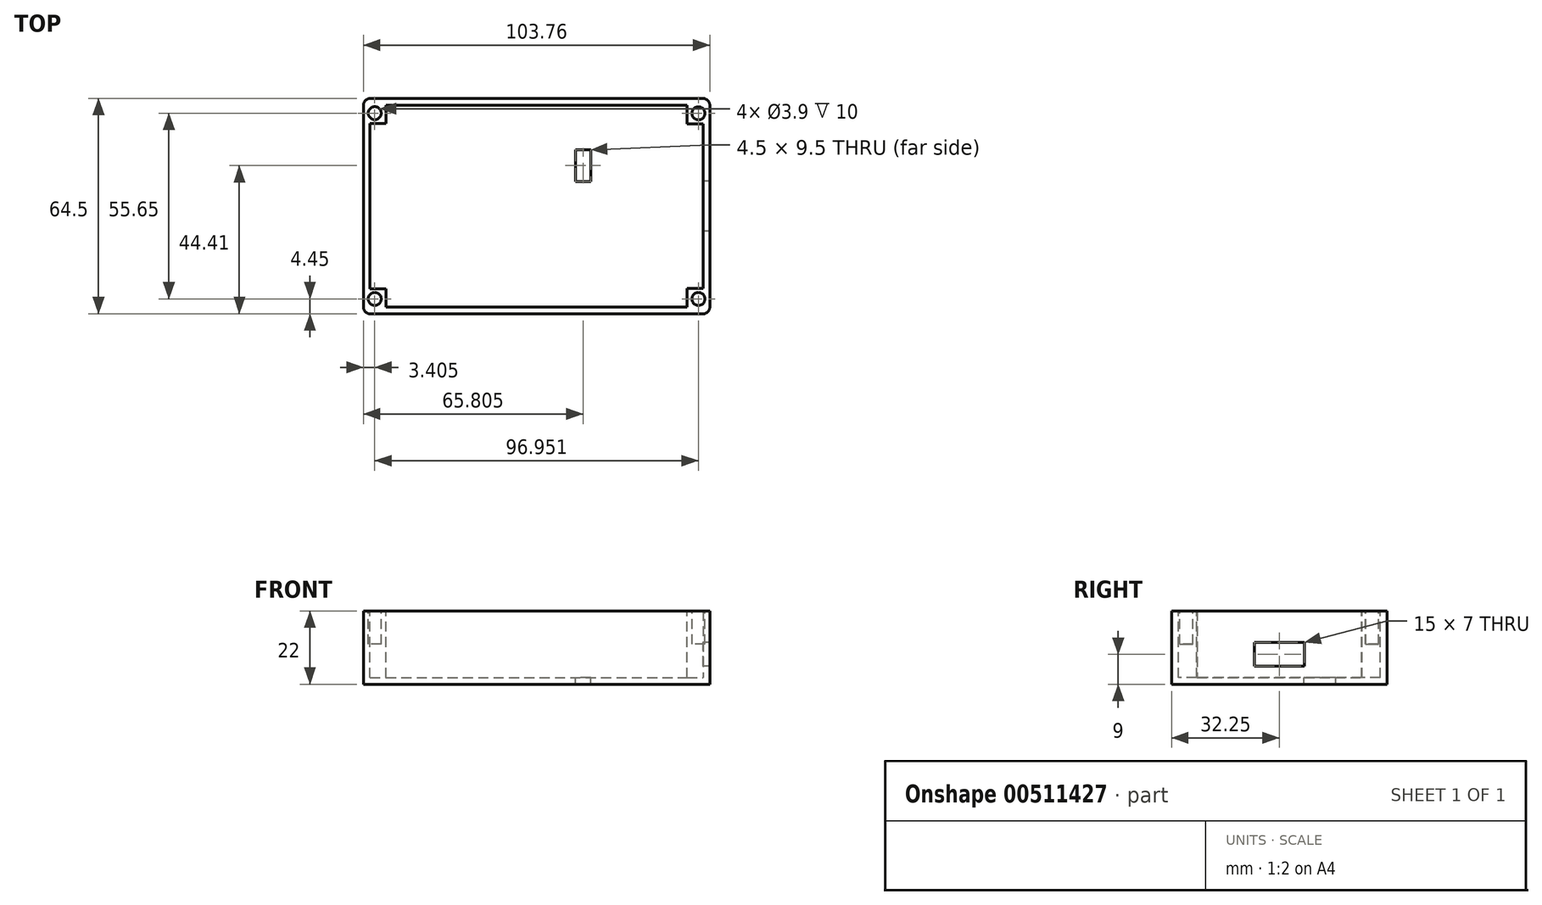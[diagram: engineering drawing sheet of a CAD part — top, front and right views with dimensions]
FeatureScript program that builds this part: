
annotation { "Feature Type Name" : "Feature", "Feature Type Description" : "" }
export const myFeature = defineFeature(function(context is Context, id is Id, definition is map)
    precondition{}
    {
        {
            var Q0;
            Q0=qCreatedBy(makeId("Top.planeOp"),FACE);
            var sketch = newSketch(context, id + "F0", { "sketchPlane" : qUnion([Q0])});
            skLineSegment(sketch, "E0.bottom", {"start": v(-51.88, 32.25) * mm, "end": v(51.88, 32.25) * mm});
            skLineSegment(sketch, "E0.top", {"start": v(-51.88, -32.25) * mm, "end": v(51.88, -32.25) * mm});
            skLineSegment(sketch, "E0.left", {"start": v(-51.88, 32.25) * mm, "end": v(-51.88, -32.25) * mm});
            skLineSegment(sketch, "E0.right", {"start": v(51.88, 32.25) * mm, "end": v(51.88, -32.25) * mm});
            skPoint(sketch, "E0.middle", {"position": v(0, 0) * mm});
            skPoint(sketch, "E1", {"position": v(-51.88, 0) * mm});
            skSolve(sketch);
        }
        {
            var Q0;
            Q0=makeQuery(id+"F0.imprint","IMPRINT",FACE,{"disambiguationData":[TD([[makeQuery(id+"F0.imprint","IMPRINT",EDGE,{"derivedFrom":sQuery(id+"F0.wireOp",EDGE,"E0.bottom")}),-1.0]])]});
            extrude(context, id + "F1", {"entities" : qUnion([Q0]), "depth" : 22 * mm});
        }
        {
            var Q0;
            Q0=makeQuery(id+"F1.opExtrude","CAP_FACE",FACE,{"disambiguationData":[OSD([sQuery(id+"F0.wireOp",EDGE,"E0.bottom"),sQuery(id+"F0.wireOp",EDGE,"E0.top"),sQuery(id+"F0.wireOp",EDGE,"E0.left"),sQuery(id+"F0.wireOp",EDGE,"E0.right")])],"isStart":false});
            shell(context, id + "F2", {"entities" : qUnion([Q0]), "thickness" : 2 * mm});
        }
        {
            var Q0;
            Q0=qCreatedBy(makeId("Right.planeOp"),FACE);
            var sketch = newSketch(context, id + "F3", { "sketchPlane" : qUnion([Q0])});
            skLineSegment(sketch, "E2.bottom", {"start": v(7.5, 12.5) * mm, "end": v(-7.5, 12.5) * mm});
            skLineSegment(sketch, "E2.top", {"start": v(7.5, 5.5) * mm, "end": v(-7.5, 5.5) * mm});
            skLineSegment(sketch, "E2.left", {"start": v(7.5, 12.5) * mm, "end": v(7.5, 5.5) * mm});
            skLineSegment(sketch, "E2.right", {"start": v(-7.5, 12.5) * mm, "end": v(-7.5, 5.5) * mm});
            skPoint(sketch, "E3", {"position": v(7.5, 9) * mm});
            skPoint(sketch, "E4", {"position": v(0, 5.5) * mm});
            skSolve(sketch);
        }
        {
            var Q0;
            Q0=qSketchRegion(id+"F3",true);
            extrude(context, id + "F4", {"entities" : qUnion([Q0]), "operationType" : NewBodyOperationType.REMOVE, "depth" : 381 * mm});
        }
        {
            var Q0;
            Q0=makeQuery(id+"F1.opExtrude","SWEPT_EDGE",EDGE,{"disambiguationData":[OSD([sQuery(id+"F0.wireOp",EDGE,"E0.bottom"),sQuery(id+"F0.wireOp",EDGE,"E0.left")])]});
            var Q1;
            Q1=makeQuery(id+"F1.opExtrude","SWEPT_EDGE",EDGE,{"disambiguationData":[OSD([sQuery(id+"F0.wireOp",EDGE,"E0.top"),sQuery(id+"F0.wireOp",EDGE,"E0.left")])]});
            var Q2;
            Q2=makeQuery(id+"F1.opExtrude","SWEPT_EDGE",EDGE,{"disambiguationData":[OSD([sQuery(id+"F0.wireOp",EDGE,"E0.top"),sQuery(id+"F0.wireOp",EDGE,"E0.right")])]});
            var Q3;
            Q3=makeQuery(id+"F1.opExtrude","SWEPT_EDGE",EDGE,{"disambiguationData":[OSD([sQuery(id+"F0.wireOp",EDGE,"E0.bottom"),sQuery(id+"F0.wireOp",EDGE,"E0.right")])]});
            fillet(context, id + "F5", {"entities" : qUnion([Q0, Q1, Q2, Q3]), "radius" : 2 * mm, "tangentPropagation" : true, "allowEdgeOverflow" : false});
        }
        {
            var Q0;
            Q0=qCreatedBy(makeId("Top.planeOp"),FACE);
            var sketch = newSketch(context, id + "F6", { "sketchPlane" : qUnion([Q0])});
            skPoint(sketch, "E5", {"position": v(-49.87, 0) * mm});
            skLineSegment(sketch, "E6.bottom", {"start": v(16.18, 16.9) * mm, "end": v(11.68, 16.9) * mm});
            skLineSegment(sketch, "E6.top", {"start": v(16.18, 7.4) * mm, "end": v(11.68, 7.4) * mm});
            skLineSegment(sketch, "E6.left", {"start": v(16.18, 16.9) * mm, "end": v(16.18, 7.4) * mm});
            skLineSegment(sketch, "E6.right", {"start": v(11.68, 16.9) * mm, "end": v(11.68, 7.4) * mm});
            skLineSegment(sketch, "E7", {"start": v(11.68, 16.9) * mm, "end": v(-49.87, 16.9) * mm});
            skSolve(sketch);
        }
        {
            var Q0;
            Q0=qSketchRegion(id+"F6",true);
            extrude(context, id + "F7", {"entities" : qUnion([Q0]), "operationType" : NewBodyOperationType.REMOVE, "endBound" : BoundingType.SYMMETRIC, "oppositeDirection" : true, "depth" : 25.4 * mm});
        }
        {
            var Q0;
            Q0=makeQuery(id+"F1.opExtrude","CAP_FACE",FACE,{"disambiguationData":[OSD([sQuery(id+"F0.wireOp",EDGE,"E0.bottom"),sQuery(id+"F0.wireOp",EDGE,"E0.top"),sQuery(id+"F0.wireOp",EDGE,"E0.left"),sQuery(id+"F0.wireOp",EDGE,"E0.right")])],"isStart":false});
            var sketch = newSketch(context, id + "F8", { "sketchPlane" : qUnion([Q0])});
            skLineSegment(sketch, "E8.bottom", {"start": v(-49.88, 30.25) * mm, "end": v(-45.08, 30.25) * mm});
            skLineSegment(sketch, "E8.top", {"start": v(-49.88, 24.75) * mm, "end": v(-45.08, 24.75) * mm});
            skLineSegment(sketch, "E8.left", {"start": v(-49.88, 30.25) * mm, "end": v(-49.88, 24.75) * mm});
            skLineSegment(sketch, "E8.right", {"start": v(-45.08, 30.25) * mm, "end": v(-45.08, 24.75) * mm});
            skLineSegment(sketch, "E9.bottom", {"start": v(45.08, 30.25) * mm, "end": v(49.88, 30.25) * mm});
            skLineSegment(sketch, "E9.top", {"start": v(45.08, 24.65) * mm, "end": v(49.88, 24.65) * mm});
            skLineSegment(sketch, "E9.left", {"start": v(45.08, 30.25) * mm, "end": v(45.08, 24.65) * mm});
            skLineSegment(sketch, "E9.right", {"start": v(49.88, 30.25) * mm, "end": v(49.88, 24.65) * mm});
            skLineSegment(sketch, "E10.bottom", {"start": v(-49.88, -24.75) * mm, "end": v(-45.08, -24.75) * mm});
            skLineSegment(sketch, "E10.top", {"start": v(-49.88, -30.25) * mm, "end": v(-45.08, -30.25) * mm});
            skLineSegment(sketch, "E10.left", {"start": v(-49.88, -24.75) * mm, "end": v(-49.88, -30.25) * mm});
            skLineSegment(sketch, "E10.right", {"start": v(-45.08, -24.75) * mm, "end": v(-45.08, -30.25) * mm});
            skLineSegment(sketch, "E11.bottom", {"start": v(45.07, -24.65) * mm, "end": v(49.87, -24.65) * mm});
            skLineSegment(sketch, "E11.top", {"start": v(45.07, -30.25) * mm, "end": v(49.87, -30.25) * mm});
            skLineSegment(sketch, "E11.left", {"start": v(45.07, -24.65) * mm, "end": v(45.07, -30.25) * mm});
            skLineSegment(sketch, "E11.right", {"start": v(49.87, -24.65) * mm, "end": v(49.87, -30.25) * mm});
            skSolve(sketch);
        }
        {
            var Q0;
            Q0 = qSketchRegion(id + "F8", true);
            extrude(context, id + "F9", {"entities" : qUnion([Q0]), "operationType" : NewBodyOperationType.ADD, "oppositeDirection" : true, "depth" : 20 * mm});
        }
        {
            var Q0;
            Q0=makeQuery(id+"F9.boolean.opBoolean","MERGE",FACE,{"derivedFrom":[makeQuery(id+"F1.opExtrude","CAP_FACE",FACE,{"disambiguationData":[OSD([sQuery(id+"F0.wireOp",EDGE,"E0.bottom"),sQuery(id+"F0.wireOp",EDGE,"E0.top"),sQuery(id+"F0.wireOp",EDGE,"E0.left"),sQuery(id+"F0.wireOp",EDGE,"E0.right")])],"isStart":false}),makeQuery(id+"F9.opExtrude","CAP_FACE",FACE,{"disambiguationData":[OSD([sQuery(id+"F8.wireOp",EDGE,"E8.bottom"),sQuery(id+"F8.wireOp",EDGE,"E8.top"),sQuery(id+"F8.wireOp",EDGE,"E8.left"),sQuery(id+"F8.wireOp",EDGE,"E8.right")])],"isStart":true}),makeQuery(id+"F9.opExtrude","CAP_FACE",FACE,{"disambiguationData":[OSD([sQuery(id+"F8.wireOp",EDGE,"E9.bottom"),sQuery(id+"F8.wireOp",EDGE,"E9.top"),sQuery(id+"F8.wireOp",EDGE,"E9.left"),sQuery(id+"F8.wireOp",EDGE,"E9.right")])],"isStart":true}),makeQuery(id+"F9.opExtrude","CAP_FACE",FACE,{"disambiguationData":[OSD([sQuery(id+"F8.wireOp",EDGE,"E10.bottom"),sQuery(id+"F8.wireOp",EDGE,"E10.top"),sQuery(id+"F8.wireOp",EDGE,"E10.left"),sQuery(id+"F8.wireOp",EDGE,"E10.right")])],"isStart":true}),makeQuery(id+"F9.opExtrude","CAP_FACE",FACE,{"disambiguationData":[OSD([sQuery(id+"F8.wireOp",EDGE,"E11.bottom"),sQuery(id+"F8.wireOp",EDGE,"E11.top"),sQuery(id+"F8.wireOp",EDGE,"E11.left"),sQuery(id+"F8.wireOp",EDGE,"E11.right")])],"isStart":true})]});
            var sketch = newSketch(context, id + "F10", { "sketchPlane" : qUnion([Q0])});
            skCircle(sketch, "E12", {"center": v(-48.48, 27.85) * mm, "radius": 1.95 * mm});
            skPoint(sketch, "E12.centerSnap0", {"position": v(-48.48, 31.26) * mm});
            skPoint(sketch, "E12.centerSnap1", {"position": v(-51.88, 27.85) * mm});
            skCircle(sketch, "E13", {"center": v(48.48, 27.8) * mm, "radius": 1.95 * mm});
            skCircle(sketch, "E14", {"center": v(-48.48, -27.8) * mm, "radius": 1.95 * mm});
            skCircle(sketch, "E15", {"center": v(48.48, -27.8) * mm, "radius": 1.95 * mm});
            skLineSegment(sketch, "E16", {"start": v(-48.48, -29.75) * mm, "end": v(-48.48, -32.25) * mm});
            skLineSegment(sketch, "E17", {"start": v(48.48, -29.75) * mm, "end": v(48.48, -32.25) * mm});
            skLineSegment(sketch, "E18", {"start": v(48.48, 29.75) * mm, "end": v(48.48, 32.25) * mm});
            skSolve(sketch);
        }
        {
            var Q0;
            Q0 = qSketchRegion(id + "F10", true);
            extrude(context, id + "F11", {"entities" : qUnion([Q0]), "operationType" : NewBodyOperationType.REMOVE, "oppositeDirection" : true, "depth" : 10 * mm});
        }
    });
